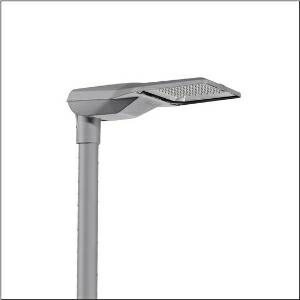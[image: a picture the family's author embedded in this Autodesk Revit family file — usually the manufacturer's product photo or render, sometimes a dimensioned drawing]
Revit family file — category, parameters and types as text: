
# Revit family: streetlight_sl_21_iq_midi___stw1_0a_5xe3e61d08nb_dcea
name_source: partatom
category: Lighting Fixtures
units: mm (PartAtom-declared; Revit-internal decimal feet)

## family parameters
Cut with Voids When Loaded = No
Host = Face
Light Source = No
Part Type = Normal
Room Calculation Point = No
Round Connector Dimension = Use Diameter
Shared = No

## types (1)
- --- (1 x LED, 20820 lm, 155.5 W, 2700K)
    Apparent Load = 155 VA
    CIE Flux Codes = 39 75 98 100 100
    Color Rendering = 70
    Color Temperature = 2700K
    Default Elevation = 1800 mm
    Description = Streetlight SL 21 iQ midi, mast luminaire, primary light control with lens, of PMMA, primary optical cover: cover, of toughened safety glass, transparent, light distribution: STW1.0a, light emission: direct distribution, primary light characteristic: asymmetric, installation type: post-top, side-entry, LED, High Power LED, rated luminous flux: 20.820lm, luminous efficacy: 134lm/W, light colour: 727, colour temperature: 2700K, control gear: iQ-Comfort, control: Auto-Match, Temp-Guard, Lumen-Switch, Night-Set, Smart-Wire, Light-Fading, Desk-Remote (wireless, voltage-free reading and setting of iQ features in the workshop via application-optimized NFC function/RFID function), optimised constant luminous flux control (CLO 2.0), pre-setting: linear dimming characteristic, mains connection: 230..240V, AC, 50/60Hz, start of lifetime: 156W, end of service life: 162W, reduction: 69W, luminaire housing, of diecast aluminium, powder-coated, SITECO metallic grey (DB 702S), corrosivity category C5 high according to DIN EN ISO 12944, please order mast flange separately, inclination adjustable: 0°, 5°, 10°, 15°, sealing non-destructively replaceable, multi-level sealing system, length: 644mm, width: 335mm, height: 110mm, mast flange for spigot size: 42mm (side-entry): 5XC10008XM4, 60/48mm (side-entry/post-top): 5XC10108XM2, 76/60mm (side-entry/post-top): 5XC10108XM1, mounting height: 4..8m, protection rating (complete): IP66, insulation class (complete): insulation class II (safety insulation), certification: CE, ENEC, ENEC+, VDE, impact resistance: IK10, permissible operating ambient temperature for outdoor applications: -40..+50°C, standard-compliant lighting for roads and squares, packaging unit: 1 piece

Light Distribution: STW1.0a
    Height = 111 mm
    Lamp = 1 x LED
    Lamp Light Flux = 20820 lm
    Lamp Power = 155.5 W
    Lamp count = 1
    Length = 644 mm
    Luminous efficacy = 134 lm/W
    Manufacturer = Siteco
    ModVariant = No
    Model = 5XE3E61D08NB
    Number of Poles = 1
    OnlyDefault = Yes
    Power Factor = 1
    Product Name = Streetlight SL 21 iQ midi | STW1.0a
    Product group = mast luminaire | pylon top
    ProductGroupID = 6100
    Protection Class = Protection class II
    Protection Degree = IP 66
    RLX_Detail_Level = 1
    RLX_Emergency_Light_Flux = 0 lm
    RLX_Emergency_Type = 0
    RLX_Emergency_Type_DB = No
    RlxData = <blob elided: 27217 chars, md5=fe39d289>
    Socket = socket
    Standby Power = 0 W
    System Light Flux = 20820 lm
    System Power = 155 W
    Type Comments = factory setting: luminous flux: 100 % | dim-lin: 254 | 823 mA
    Type Image = l_1004298.jpg
    URL = http://relux.com
    VarID = @adj_169241
    Voltage = 0 V
    Weight = 0.00 kg
    Width = 336 mm

## geometry (parser evidence)
native form markers: Blend x4, Sweep x10
no freeform markers — native parametric forms only
